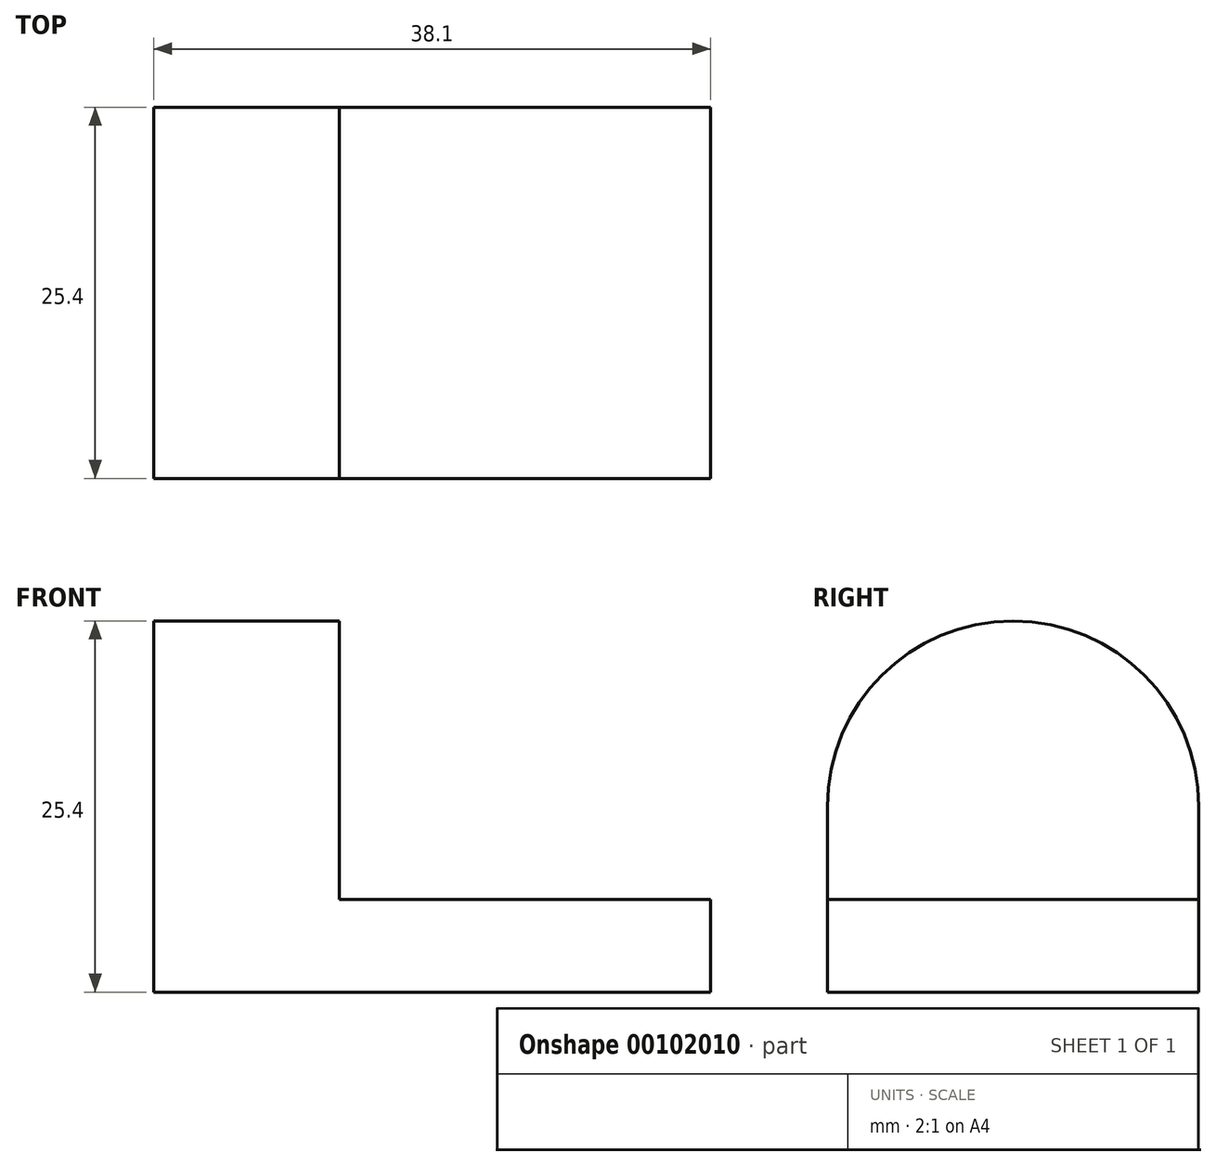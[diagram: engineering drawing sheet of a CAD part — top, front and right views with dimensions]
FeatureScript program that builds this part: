
annotation { "Feature Type Name" : "Feature", "Feature Type Description" : "" }
export const myFeature = defineFeature(function(context is Context, id is Id, definition is map)
    precondition{}
    {
        {
            var Q0;
            Q0=qCreatedBy(makeId("Right.planeOp"),FACE);
            var sketch = newSketch(context, id + "F0", { "sketchPlane" : qUnion([Q0])});
            skLineSegment(sketch, "E0", {"start": v(0, 0) * mm, "end": v(25.4, 0) * mm});
            skLineSegment(sketch, "E1", {"start": v(25.4, 0) * mm, "end": v(25.4, 12.7) * mm});
            skLineSegment(sketch, "E2", {"start": v(0, 12.7) * mm, "end": v(0, 0) * mm});
            skArc(sketch, "E3", {"start": v(25.4, 12.7) * mm, "mid": v(12.7, 25.4) * mm, "end": v(0, 12.7) * mm});
            skSolve(sketch);
        }
        {
            var Q0;
            Q0 = qSketchRegion(id + "F0", true);
            extrude(context, id + "F1", {"entities" : qUnion([Q0]), "endBound" : BoundingType.SYMMETRIC, "depth" : 12.7 * mm});
        }
        {
            var Q0;
            Q0=qCreatedBy(makeId("Right.planeOp"),FACE);
            var sketch = newSketch(context, id + "F2", { "sketchPlane" : qUnion([Q0])});
            skLineSegment(sketch, "E4", {"start": v(0, 0) * mm, "end": v(25.4, 0) * mm});
            skLineSegment(sketch, "E5", {"start": v(25.4, 0) * mm, "end": v(25.4, 6.35) * mm});
            skLineSegment(sketch, "E6", {"start": v(25.4, 6.35) * mm, "end": v(0, 6.35) * mm});
            skLineSegment(sketch, "E7", {"start": v(0, 6.35) * mm, "end": v(0, 0) * mm});
            skSolve(sketch);
        }
        {
            var Q0;
            Q0 = qSketchRegion(id + "F2", true);
            extrude(context, id + "F3", {"entities" : qUnion([Q0]), "operationType" : NewBodyOperationType.ADD, "depth" : 31.75 * mm});
        }
    });
